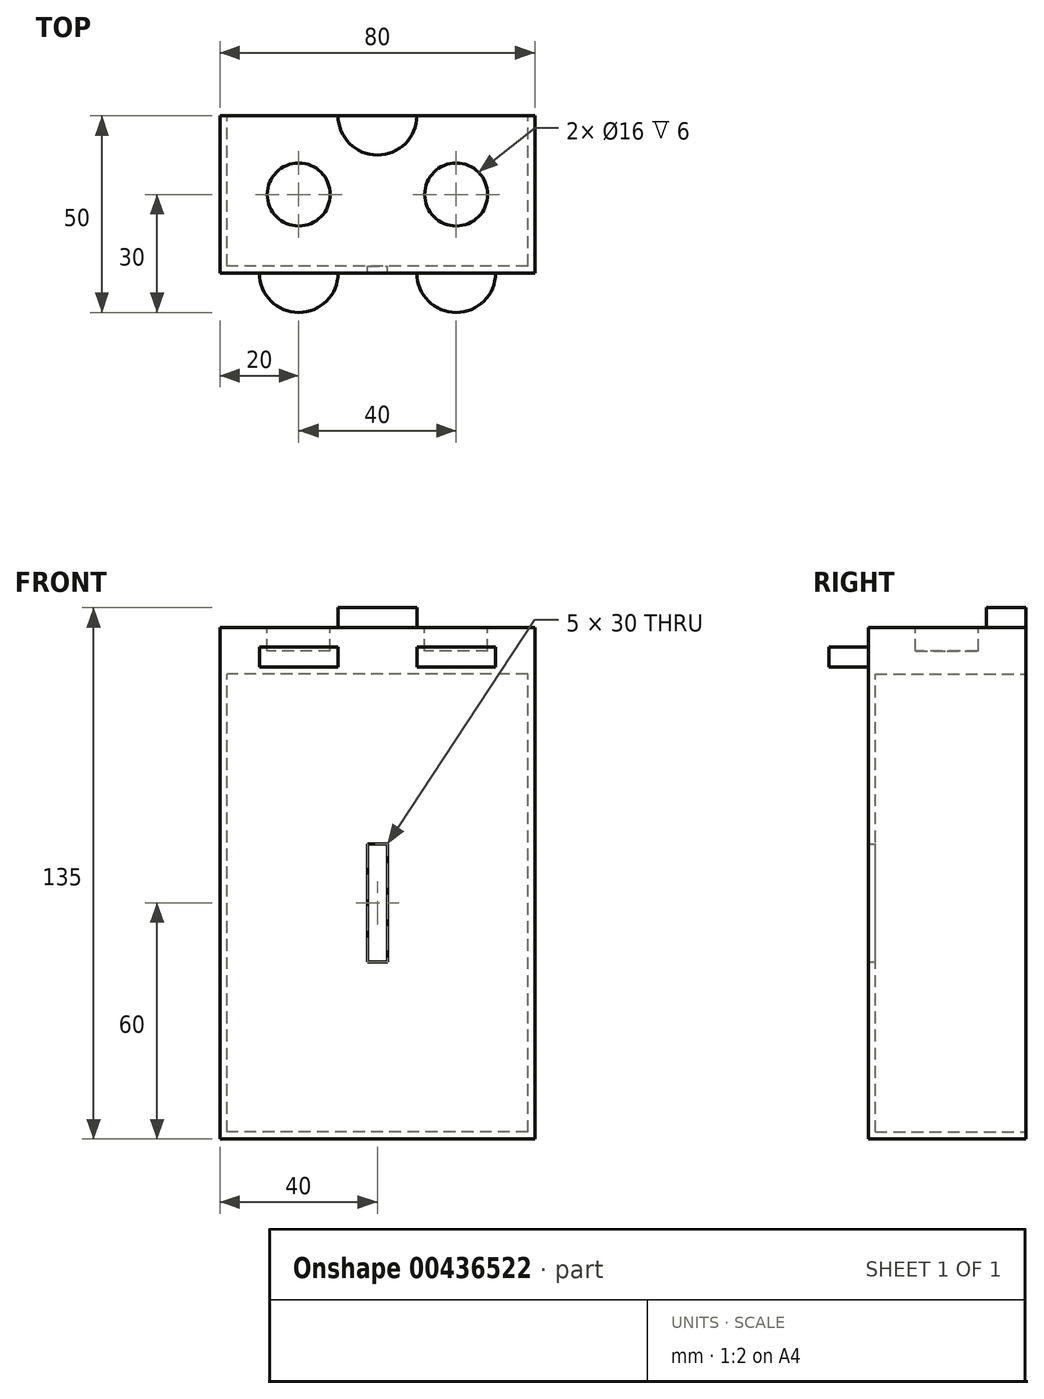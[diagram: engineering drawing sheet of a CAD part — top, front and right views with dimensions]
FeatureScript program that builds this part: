
annotation { "Feature Type Name" : "Feature", "Feature Type Description" : "" }
export const myFeature = defineFeature(function(context is Context, id is Id, definition is map)
    precondition{}
    {
        {
            var Q0;
            Q0=qCreatedBy(makeId("Front.planeOp"),FACE);
            var sketch = newSketch(context, id + "F0", { "sketchPlane" : qUnion([Q0])});
            skLineSegment(sketch, "E0.bottom", {"start": v(0, 0) * mm, "end": v(-80, 0) * mm});
            skLineSegment(sketch, "E0.top", {"start": v(0, 120) * mm, "end": v(-80, 120) * mm});
            skLineSegment(sketch, "E0.left", {"start": v(0, 0) * mm, "end": v(0, 120) * mm});
            skLineSegment(sketch, "E0.right", {"start": v(-80, 0) * mm, "end": v(-80, 120) * mm});
            skLineSegment(sketch, "E1.top", {"start": v(0, 130) * mm, "end": v(-80, 130) * mm});
            skLineSegment(sketch, "E1.left", {"start": v(0, 120) * mm, "end": v(0, 130) * mm});
            skLineSegment(sketch, "E1.right", {"start": v(-80, 120) * mm, "end": v(-80, 130) * mm});
            skSolve(sketch);
        }
        {
            var Q0;
            Q0=makeQuery(id+"F0.imprint","IMPRINT",FACE,{"disambiguationData":[TD([[makeQuery(id+"F0.imprint","IMPRINT",EDGE,{"derivedFrom":sQuery(id+"F0.wireOp",EDGE,"E0.bottom")}),-1.0]])]});
            extrude(context, id + "F1", {"entities" : qUnion([Q0]), "depth" : 40 * mm});
        }
        {
            var Q0;
            Q0=makeQuery(id+"F1.opExtrude","CAP_FACE",FACE,{"disambiguationData":[OSD([sQuery(id+"F0.wireOp",EDGE,"E0.bottom"),sQuery(id+"F0.wireOp",EDGE,"E0.left"),sQuery(id+"F0.wireOp",EDGE,"E0.right"),sQuery(id+"F0.wireOp",EDGE,"E0.top")])],"isStart":true});
            shell(context, id + "F2", {"entities" : qUnion([Q0]), "thickness" : 1.8 * mm});
        }
        {
            var Q0;
            Q0=makeQuery(id+"F0.imprint","IMPRINT",FACE,{"disambiguationData":[TD([[makeQuery(id+"F0.imprint","IMPRINT",EDGE,{"derivedFrom":sQuery(id+"F0.wireOp",EDGE,"E0.top")}),-1.0]])]});
            extrude(context, id + "F3", {"entities" : qUnion([Q0]), "operationType" : NewBodyOperationType.ADD, "depth" : 40 * mm});
        }
        {
            var Q0;
            Q0=makeQuery(id+"F0.imprint","IMPRINT",FACE,{"disambiguationData":[TD([[makeQuery(id+"F0.imprint","IMPRINT",EDGE,{"derivedFrom":sQuery(id+"F0.wireOp",EDGE,"E0.bottom")}),-1.0]])]});
            var sketch = newSketch(context, id + "F4", { "sketchPlane" : qUnion([Q0])});
            skLineSegment(sketch, "E2.bottom", {"start": v(0, 0) * mm, "end": v(-40, 0) * mm});
            skLineSegment(sketch, "E2.top", {"start": v(0, 0) * mm, "end": v(-40, 0) * mm});
            skLineSegment(sketch, "E2.left", {"start": v(0, 0) * mm, "end": v(0, 0) * mm});
            skLineSegment(sketch, "E2.right", {"start": v(-40, 0) * mm, "end": v(-40, 0) * mm});
            skLineSegment(sketch, "E3", {"start": v(-40, 0) * mm, "end": v(-40, 60) * mm});
            skLineSegment(sketch, "E4.bottom", {"start": v(-37.5, 75) * mm, "end": v(-42.5, 75) * mm});
            skLineSegment(sketch, "E4.top", {"start": v(-37.5, 45) * mm, "end": v(-42.5, 45) * mm});
            skLineSegment(sketch, "E4.left", {"start": v(-37.5, 75) * mm, "end": v(-37.5, 45) * mm});
            skLineSegment(sketch, "E4.right", {"start": v(-42.5, 75) * mm, "end": v(-42.5, 45) * mm});
            skPoint(sketch, "E4.middle", {"position": v(-40, 60) * mm});
            skSolve(sketch);
        }
        {
            var Q0;
            Q0=makeQuery(id+"F4.imprint","IMPRINT",FACE,{"disambiguationData":[TD([[makeQuery(id+"F4.imprint","IMPRINT",EDGE,{"derivedFrom":sQuery(id+"F4.wireOp",EDGE,"E4.bottom")}),1.0]])]});
            extrude(context, id + "F5", {"entities" : qUnion([Q0]), "operationType" : NewBodyOperationType.REMOVE, "depth" : 40 * mm});
        }
        {
            var Q0;
            Q0=qCreatedBy(makeId("Top.planeOp"),FACE);
            cPlane(context, id + "F6", {"entities" : qUnion([Q0]), "cplaneType" : CPlaneType.OFFSET, "offset" : 130 * mm, "width" : 150 * mm, "height" : 150 * mm});
        }
        {
            var Q0;
            Q0=qCreatedBy(id+"F6.planeOp",FACE);
            var sketch = newSketch(context, id + "F7", { "sketchPlane" : qUnion([Q0])});
            skLineSegment(sketch, "E5", {"start": v(0, 0) * mm, "end": v(-40, 0) * mm});
            skLineSegment(sketch, "E6", {"start": v(-40, 0) * mm, "end": v(-60, 0) * mm});
            skLineSegment(sketch, "E7", {"start": v(0, 0) * mm, "end": v(-15.2, 0) * mm});
            skLineSegment(sketch, "E8", {"start": v(0, 0) * mm, "end": v(-20, 0) * mm});
            skLineSegment(sketch, "E9", {"start": v(-20, 0) * mm, "end": v(-20, -12) * mm});
            skLineSegment(sketch, "E10", {"start": v(-60, 0) * mm, "end": v(-60, -12) * mm});
            skCircle(sketch, "E11", {"center": v(-40, 0) * mm, "radius": 10 * mm});
            skCircle(sketch, "E12", {"center": v(-60, -20) * mm, "radius": 8 * mm});
            skCircle(sketch, "E13", {"center": v(-20, -20) * mm, "radius": 8 * mm});
            skLineSegment(sketch, "E14", {"start": v(-60, -20) * mm, "end": v(-60, -40) * mm});
            skLineSegment(sketch, "E15", {"start": v(-20, -20) * mm, "end": v(-20, -40) * mm});
            skCircle(sketch, "E16", {"center": v(-60, -40) * mm, "radius": 10 * mm});
            skCircle(sketch, "E17", {"center": v(-20, -40) * mm, "radius": 10 * mm});
            skSolve(sketch);
        }
        {
            var Q0;
            {var subQ0=sQuery(id+"F7.wireOp",EDGE,"E6");var subQ1=sQuery(id+"F7.wireOp",EDGE,"E5");var subQ2=makeQuery(id+"F7.imprint","INTERSECT",VERTEX,{"derivedFrom":[subQ1,subQ0]});Q0=makeQuery(id+"F7.imprint","IMPRINT",FACE,{"disambiguationData":[TD([[makeQuery(id+"F7.imprint","IMPRINT",EDGE,{"disambiguationData":[TD([[subQ2,1.0]])],"derivedFrom":subQ1}),1.0]])]});}
            extrude(context, id + "F8", {"entities" : qUnion([Q0]), "operationType" : NewBodyOperationType.ADD, "depth" : 5 * mm});
        }
        {
            var Q0;
            Q0=makeQuery(id+"F7.imprint","IMPRINT",FACE,{"disambiguationData":[TD([[makeQuery(id+"F7.imprint","IMPRINT",EDGE,{"derivedFrom":sQuery(id+"F7.wireOp",EDGE,"E13")}),1.0]])]});
            var Q1;
            Q1=makeQuery(id+"F7.imprint","IMPRINT",FACE,{"disambiguationData":[TD([[makeQuery(id+"F7.imprint","IMPRINT",EDGE,{"derivedFrom":sQuery(id+"F7.wireOp",EDGE,"E12")}),1.0]])]});
            extrude(context, id + "F9", {"entities" : qUnion([Q0, Q1]), "operationType" : NewBodyOperationType.REMOVE, "oppositeDirection" : true, "depth" : 6 * mm});
        }
        {
            var Q0;
            Q0=makeQuery(id+"F7.imprint","IMPRINT",FACE,{"disambiguationData":[TD([[makeQuery(id+"F7.imprint","IMPRINT",EDGE,{"derivedFrom":sQuery(id+"F7.wireOp",EDGE,"E16")}),1.0]])]});
            var Q1;
            Q1=makeQuery(id+"F7.imprint","IMPRINT",FACE,{"disambiguationData":[TD([[makeQuery(id+"F7.imprint","IMPRINT",EDGE,{"derivedFrom":sQuery(id+"F7.wireOp",EDGE,"E17")}),1.0]])]});
            extrude(context, id + "F10", {"entities" : qUnion([Q0, Q1]), "operationType" : NewBodyOperationType.ADD, "oppositeDirection" : true, "depth" : 10 * mm});
        }
        {
            var Q0;
            Q0=qCreatedBy(id+"F6.planeOp",FACE);
            var sketch = newSketch(context, id + "F11", { "sketchPlane" : qUnion([Q0])});
            skLineSegment(sketch, "E18", {"start": v(0, 0) * mm, "end": v(-20, 0) * mm});
            skLineSegment(sketch, "E19", {"start": v(-20, 0) * mm, "end": v(-20, -30) * mm});
            skCircle(sketch, "E20", {"center": v(-20, -40) * mm, "radius": 10 * mm});
            skLineSegment(sketch, "E21", {"start": v(-20, -40) * mm, "end": v(-60, -40) * mm});
            skCircle(sketch, "E22", {"center": v(-60, -40) * mm, "radius": 10 * mm});
            skLineSegment(sketch, "E23", {"start": v(-60, -40) * mm, "end": v(-70, -40) * mm});
            skLineSegment(sketch, "E24", {"start": v(-20, -40) * mm, "end": v(-10, -40) * mm});
            skSolve(sketch);
        }
        {
            var Q0;
            {var subQ0=sQuery(id+"F11.wireOp",EDGE,"E23");Q0=makeQuery(id+"F11.imprint","IMPRINT",FACE,{"disambiguationData":[TD([[makeQuery(id+"F11.imprint","IMPRINT",EDGE,{"derivedFrom":subQ0}),1.0]])]});}
            var Q1;
            {var subQ0=sQuery(id+"F11.wireOp",EDGE,"E24");Q1=makeQuery(id+"F11.imprint","IMPRINT",FACE,{"disambiguationData":[TD([[makeQuery(id+"F11.imprint","IMPRINT",EDGE,{"derivedFrom":subQ0}),-1.0]])]});}
            extrude(context, id + "F12", {"entities" : qUnion([Q0, Q1]), "operationType" : NewBodyOperationType.REMOVE, "oppositeDirection" : true, "depth" : 5 * mm});
        }
    });
